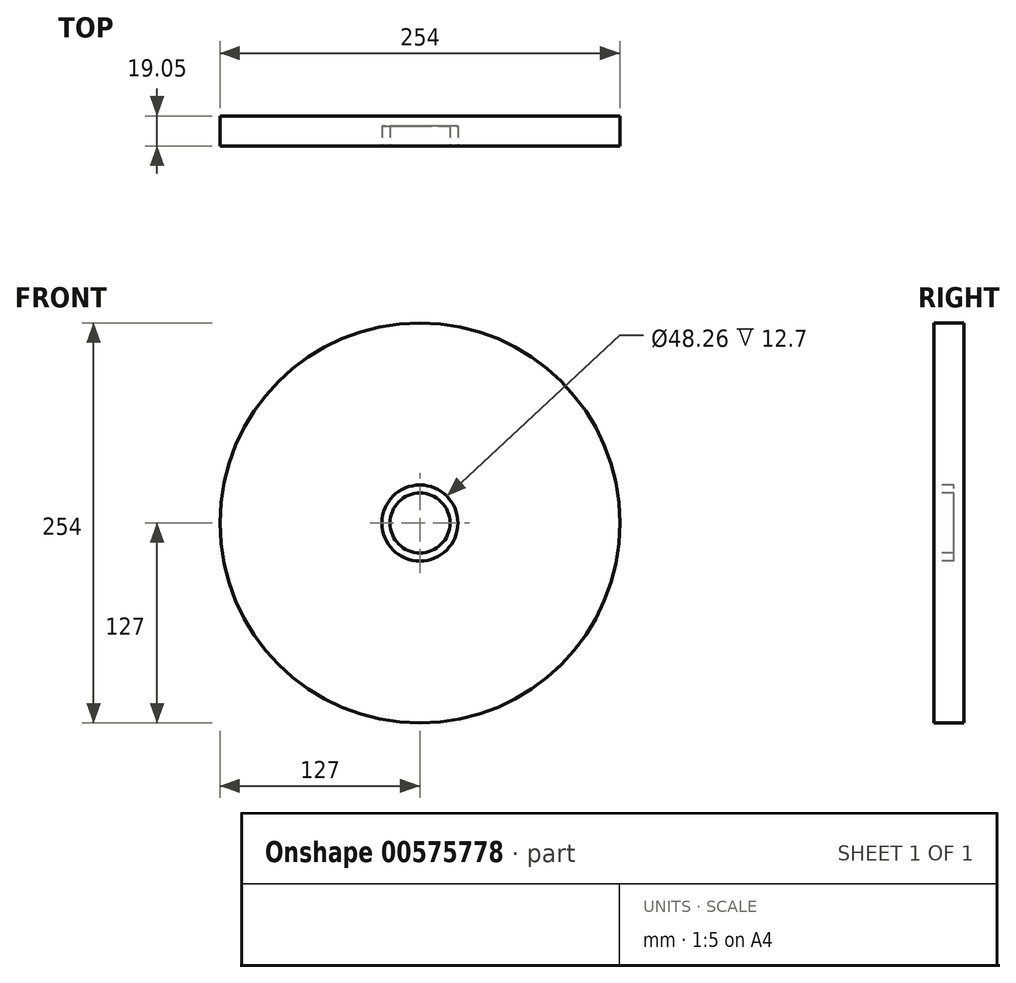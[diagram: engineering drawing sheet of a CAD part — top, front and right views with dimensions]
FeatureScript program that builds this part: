
annotation { "Feature Type Name" : "Feature", "Feature Type Description" : "" }
export const myFeature = defineFeature(function(context is Context, id is Id, definition is map)
    precondition{}
    {
        {
            var Q0;
            Q0=qCreatedBy(makeId("Front.planeOp"),FACE);
            var sketch = newSketch(context, id + "F0", { "sketchPlane" : qUnion([Q0])});
            skCircle(sketch, "E0", {"center": v(0, 0) * mm, "radius": 127 * mm});
            skCircle(sketch, "E1", {"center": v(0, 0) * mm, "radius": 24.13 * mm});
            skCircle(sketch, "E2", {"center": v(0, 0) * mm, "radius": 19.05 * mm});
            skSolve(sketch);
        }
        {
            var Q0;
            Q0=makeQuery(id+"F0.imprint","IMPRINT",FACE,{"disambiguationData":[TD([[makeQuery(id+"F0.imprint","IMPRINT",EDGE,{"derivedFrom":sQuery(id+"F0.wireOp",EDGE,"E0")}),1.0]])]});
            var Q1;
            Q1=makeQuery(id+"F0.imprint","IMPRINT",FACE,{"disambiguationData":[TD([[makeQuery(id+"F0.imprint","IMPRINT",EDGE,{"derivedFrom":sQuery(id+"F0.wireOp",EDGE,"E1")}),1.0]])]});
            var Q2;
            Q2=makeQuery(id+"F0.imprint","IMPRINT",FACE,{"disambiguationData":[TD([[makeQuery(id+"F0.imprint","IMPRINT",EDGE,{"derivedFrom":sQuery(id+"F0.wireOp",EDGE,"E2")}),1.0]])]});
            extrude(context, id + "F1", {"entities" : qUnion([Q0, Q1, Q2]), "oppositeDirection" : true, "depth" : 19.05 * mm, "offsetDistance" : 25.4 * mm});
        }
        {
            var Q0;
            Q0=makeQuery(id+"F0.imprint","IMPRINT",FACE,{"disambiguationData":[TD([[makeQuery(id+"F0.imprint","IMPRINT",EDGE,{"derivedFrom":sQuery(id+"F0.wireOp",EDGE,"E1")}),1.0]])]});
            extrude(context, id + "F2", {"entities" : qUnion([Q0]), "operationType" : NewBodyOperationType.REMOVE, "oppositeDirection" : true, "depth" : 12.7 * mm, "offsetDistance" : 25.4 * mm});
        }
    });
